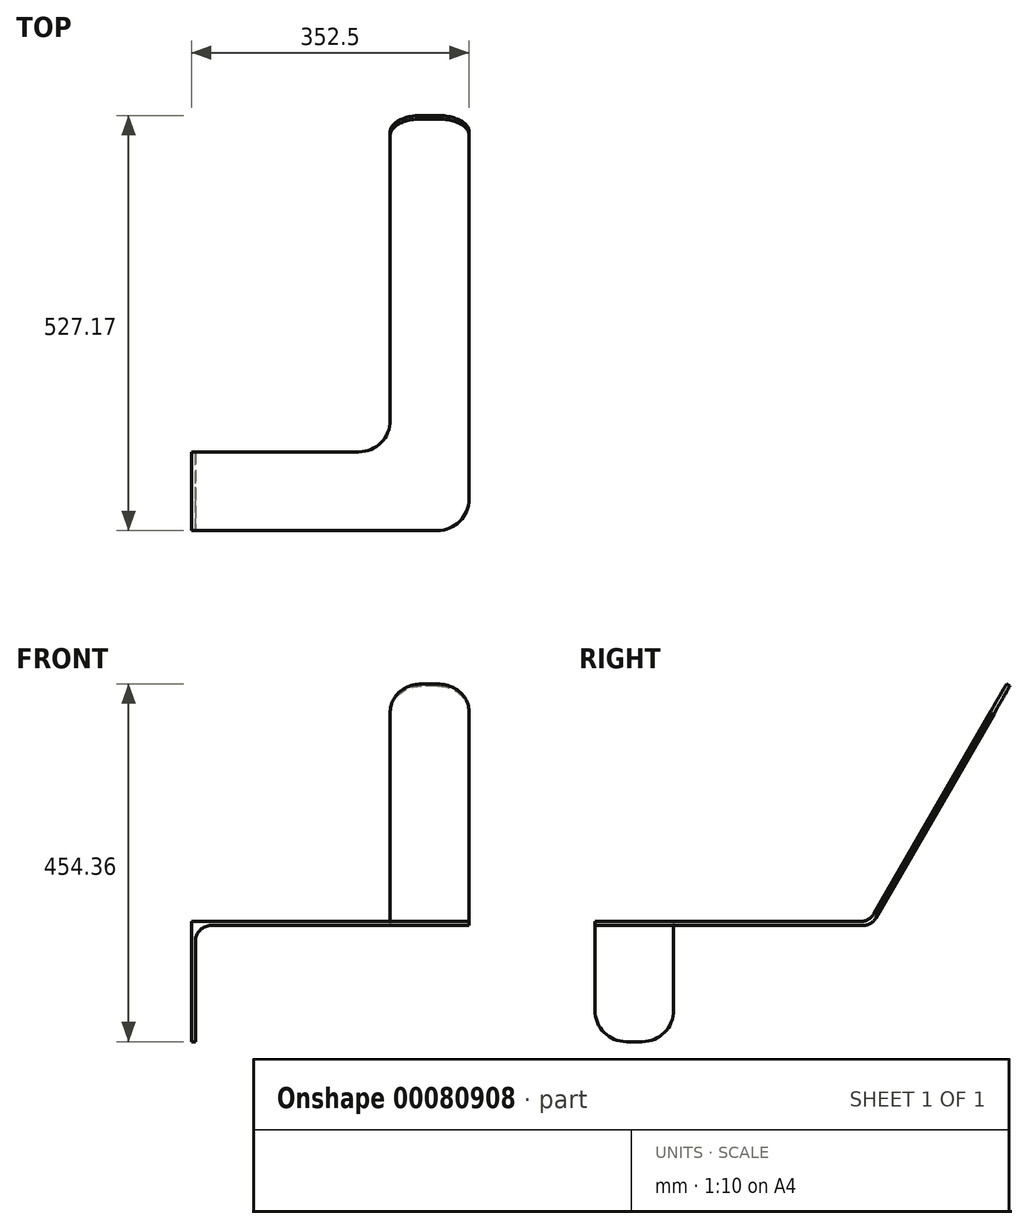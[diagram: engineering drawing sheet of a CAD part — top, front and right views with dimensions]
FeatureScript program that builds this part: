
annotation { "Feature Type Name" : "Feature", "Feature Type Description" : "" }
export const myFeature = defineFeature(function(context is Context, id is Id, definition is map)
    precondition{}
    {
        {
            var Q0;
            Q0=qCreatedBy(makeId("Front.planeOp"),FACE);
            var sketch = newSketch(context, id + "F0", { "sketchPlane" : qUnion([Q0])});
            skLineSegment(sketch, "E0", {"start": v(0, 0) * mm, "end": v(300, 0) * mm});
            skLineSegment(sketch, "E1", {"start": v(0, 0) * mm, "end": v(0, -150) * mm});
            skPoint(sketch, "E2", {"position": v(0, 0) * mm});
            skSolve(sketch);
        }
        {
            var Q0;
            Q0=qCreatedBy(makeId("Right.planeOp"),FACE);
            var Q1;
            Q1=sQuery(id+"F0.wireOp",VERTEX,"E0.end");
            cPlane(context, id + "F1", {"entities" : qUnion([Q0, Q1]), "cplaneType" : CPlaneType.PLANE_POINT, "offset" : 150 * mm, "width" : 150 * mm, "height" : 150 * mm});
        }
        {
            var Q0;
            Q0=qCreatedBy(id+"F1.planeOp",FACE);
            var sketch = newSketch(context, id + "F2", { "sketchPlane" : qUnion([Q0])});
            skLineSegment(sketch, "E3", {"start": v(0, 0) * mm, "end": v(300, 0) * mm});
            skLineSegment(sketch, "E4", {"start": v(300, 0) * mm, "end": v(475, 303.1) * mm});
            skPoint(sketch, "E5", {"position": v(450, 259.8) * mm});
            skSolve(sketch);
        }
        {
            var Q0;
            Q0=qCreatedBy(makeId("Top.planeOp"),FACE);
            var Q1;
            Q1=sQuery(id+"F0.wireOp",VERTEX,"E1.end");
            cPlane(context, id + "F3", {"entities" : qUnion([Q0, Q1]), "cplaneType" : CPlaneType.PLANE_POINT, "offset" : 150 * mm, "width" : 150 * mm, "height" : 150 * mm});
        }
        {
            var Q0;
            Q0=qCreatedBy(id+"F3.planeOp",FACE);
            var sketch = newSketch(context, id + "F4", { "sketchPlane" : qUnion([Q0])});
            skLineSegment(sketch, "E6.bottom", {"start": v(2.5, -50) * mm, "end": v(-2.5, -50) * mm});
            skLineSegment(sketch, "E6.top", {"start": v(2.5, 50) * mm, "end": v(-2.5, 50) * mm});
            skLineSegment(sketch, "E6.left", {"start": v(2.5, -50) * mm, "end": v(2.5, 50) * mm});
            skLineSegment(sketch, "E6.right", {"start": v(-2.5, -50) * mm, "end": v(-2.5, 50) * mm});
            skPoint(sketch, "E6.middle", {"position": v(0, 0) * mm});
            skSolve(sketch);
        }
        {
            var Q0;
            Q0=makeQuery(id+"F4.imprint","IMPRINT",FACE,{"disambiguationData":[TD([[makeQuery(id+"F4.imprint","IMPRINT",EDGE,{"derivedFrom":sQuery(id+"F4.wireOp",EDGE,"E6.bottom")}),-1.0]])]});
            var Q1;
            Q1=sQuery(id+"F0.wireOp",EDGE,"E1");
            var Q2;
            Q2=sQuery(id+"F0.wireOp",EDGE,"E0");
            var Q3;
            Q3=sQuery(id+"F2.wireOp",EDGE,"E3");
            var Q4;
            Q4=sQuery(id+"F2.wireOp",EDGE,"E4");
            sweep(context, id + "F5", {"profiles" : qUnion([Q0]), "path" : qUnion([Q1, Q2, Q3, Q4])});
        }
        {
            var Q0;
            Q0=makeQuery(id+"F5.opSweep","MID_CAP_EDGE",EDGE,{"disambiguationData":[OSD([sQuery(id+"F0.wireOp",VERTEX,"E0.start"),sQuery(id+"F4.wireOp",EDGE,"E6.left")])],"capPos":1.0});
            var Q1;
            Q1=makeQuery(id+"F5.opSweep","MID_CAP_EDGE",EDGE,{"disambiguationData":[OSD([sQuery(id+"F2.wireOp",VERTEX,"E4.start"),sQuery(id+"F4.wireOp",EDGE,"E6.right")])],"capPos":3.0});
            var Q2;
            Q2=makeQuery(id+"F5.opSweep","MID_CAP_EDGE",EDGE,{"disambiguationData":[OSD([sQuery(id+"F2.wireOp",VERTEX,"E4.start"),sQuery(id+"F4.wireOp",EDGE,"E6.left")])],"capPos":3.0});
            fillet(context, id + "F6", {"entities" : qUnion([Q0, Q1, Q2]), "radius" : 20 * mm, "tangentPropagation" : true, "allowEdgeOverflow" : false});
        }
        {
            var Q0;
            Q0=makeQuery(id+"F5.opSweep","MID_CAP_EDGE",EDGE,{"disambiguationData":[OSD([sQuery(id+"F2.wireOp",VERTEX,"E3.start"),sQuery(id+"F4.wireOp",EDGE,"E6.bottom")])],"capPos":2.0});
            var Q1;
            Q1=makeQuery(id+"F5.opSweep","MID_CAP_EDGE",EDGE,{"disambiguationData":[OSD([sQuery(id+"F2.wireOp",VERTEX,"E3.start"),sQuery(id+"F4.wireOp",EDGE,"E6.top")])],"capPos":2.0});
            var Q2;
            Q2=makeQuery(id+"F5.opSweep","CAP_EDGE",EDGE,{"disambiguationData":[OSD([sQuery(id+"F2.wireOp",VERTEX,"E4.end"),sQuery(id+"F4.wireOp",EDGE,"E6.bottom")])],"isStart":false});
            var Q3;
            Q3=makeQuery(id+"F5.opSweep","CAP_EDGE",EDGE,{"disambiguationData":[OSD([sQuery(id+"F2.wireOp",VERTEX,"E4.end"),sQuery(id+"F4.wireOp",EDGE,"E6.top")])],"isStart":false});
            var Q4;
            Q4=makeQuery(id+"F5.opSweep","CAP_EDGE",EDGE,{"disambiguationData":[OSD([sQuery(id+"F0.wireOp",VERTEX,"E1.end"),sQuery(id+"F4.wireOp",EDGE,"E6.bottom")])],"isStart":true});
            var Q5;
            Q5=makeQuery(id+"F5.opSweep","CAP_EDGE",EDGE,{"disambiguationData":[OSD([sQuery(id+"F0.wireOp",VERTEX,"E1.end"),sQuery(id+"F4.wireOp",EDGE,"E6.top")])],"isStart":true});
            fillet(context, id + "F7", {"entities" : qUnion([Q0, Q1, Q2, Q3, Q4, Q5]), "radius" : 40 * mm, "tangentPropagation" : true, "allowEdgeOverflow" : false});
        }
        {
            var Q0;
            Q0=qCreatedBy(makeId("Top.planeOp"),FACE);
            var sketch = newSketch(context, id + "F8", { "sketchPlane" : qUnion([Q0])});
            skPoint(sketch, "E7", {"position": v(300, 450) * mm});
            skSolve(sketch);
        }
        {
            var Q0;
            Q0=qCreatedBy(makeId("Origin.pointOp"),VERTEX);
            var Q1;
            Q1=sQuery(id+"F2.wireOp",VERTEX,"E5");
            var Q2;
            Q2=sQuery(id+"F8.wireOp",VERTEX,"E7");
            cPlane(context, id + "F9", {"entities" : qUnion([Q0, Q1, Q2]), "cplaneType" : CPlaneType.THREE_POINT, "offset" : 150 * mm, "width" : 150 * mm, "height" : 150 * mm});
        }
        {
            var Q0;
            Q0=qCreatedBy(id+"F9.planeOp",FACE);
            var sketch = newSketch(context, id + "F10", { "sketchPlane" : qUnion([Q0])});
            skLineSegment(sketch, "E8", {"start": v(0, 0) * mm, "end": v(540.83, 259.8) * mm});
            skSolve(sketch);
        }
        {
            var Q0;
            Q0=makeQuery(id+"F5.opSweep","SWEPT_FACE",FACE,{"disambiguationData":[OSD([sQuery(id+"F2.wireOp",EDGE,"E4"),sQuery(id+"F4.wireOp",EDGE,"E6.right")])]});
            var sketch = newSketch(context, id + "F11", { "sketchPlane" : qUnion([Q0])});
            skLineSegment(sketch, "E9", {"start": v(300, 450) * mm, "end": v(559.8, 600) * mm});
            skLineSegment(sketch, "E10", {"start": v(300, 450) * mm, "end": v(350, 450) * mm, "construction": true});
            skSolve(sketch);
        }
        {
            var Q0;
            Q0=sQuery(id+"F10.wireOp",VERTEX,"E8.start");
            var Q1;
            Q1=sQuery(id+"F2.wireOp",VERTEX,"E5");
            var Q2;
            Q2=sQuery(id+"F11.wireOp",VERTEX,"E9.end");
            cPlane(context, id + "F12", {"entities" : qUnion([Q0, Q1, Q2]), "cplaneType" : CPlaneType.THREE_POINT, "offset" : 150 * mm, "width" : 150 * mm, "height" : 150 * mm});
        }
    });
